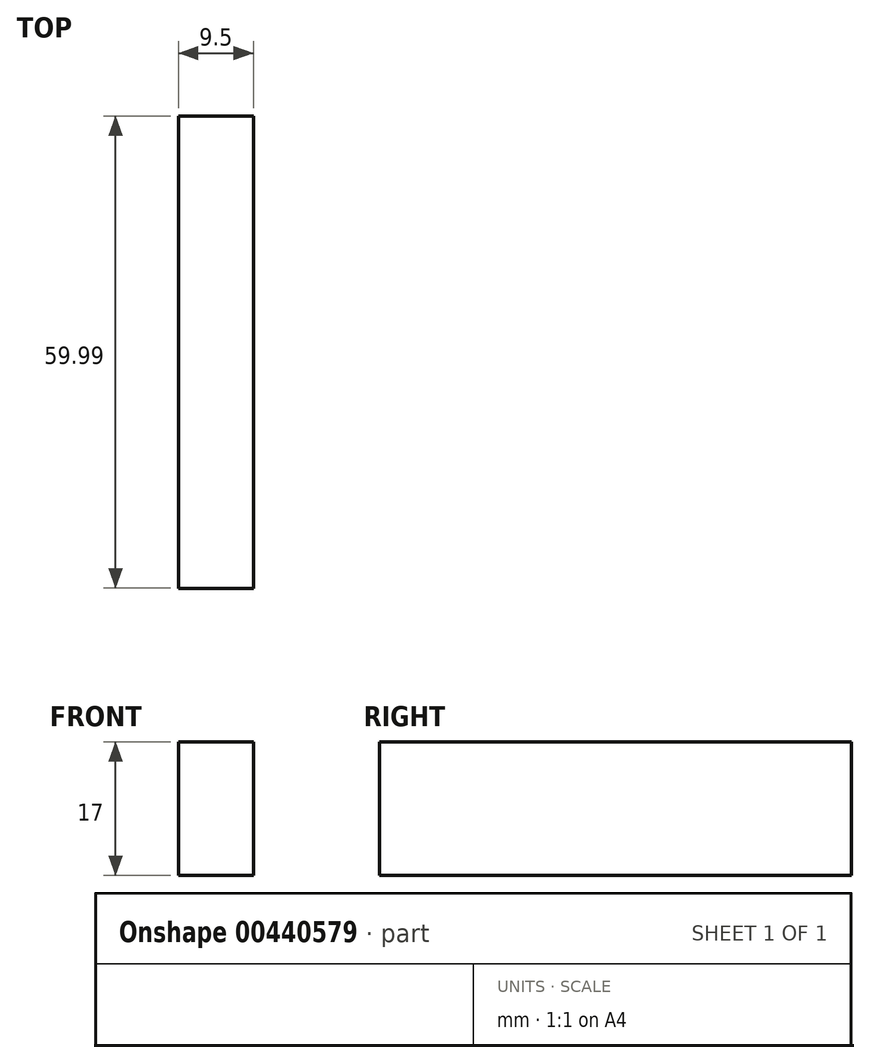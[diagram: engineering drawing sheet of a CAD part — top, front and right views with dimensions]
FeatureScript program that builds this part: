
annotation { "Feature Type Name" : "Feature", "Feature Type Description" : "" }
export const myFeature = defineFeature(function(context is Context, id is Id, definition is map)
    precondition{}
    {
        {
            var Q0;
            Q0=qCreatedBy(makeId("Top.planeOp"),FACE);
            var sketch = newSketch(context, id + "F0", { "sketchPlane" : qUnion([Q0])});
            skArc(sketch, "E0", {"start": v(-453.02, 960.92) * mm, "mid": v(90.35, 1058.5) * mm, "end": v(609.32, 870.25) * mm});
            skLineSegment(sketch, "E1", {"start": v(-465.89, 988.2) * mm, "end": v(-453.02, 960.92) * mm});
            skLineSegment(sketch, "E2", {"start": v(609.32, 870.25) * mm, "end": v(626.62, 894.95) * mm});
            skPoint(sketch, "E3.orphan", {"position": v(-465.89, 988.2) * mm});
            skArc(sketch, "E4", {"start": v(-465.89, 988.2) * mm, "mid": v(92.91, 1088.56) * mm, "end": v(626.62, 894.95) * mm});
            skSolve(sketch);
        }
        {
            var Q0;
            Q0=qCreatedBy(makeId("Top.planeOp"),FACE);
            var sketch = newSketch(context, id + "F1", { "sketchPlane" : qUnion([Q0])});
            skLineSegment(sketch, "E5.bottom", {"start": v(953.2, 454.88) * mm, "end": v(962.7, 454.88) * mm});
            skLineSegment(sketch, "E5.top", {"start": v(953.2, 394.89) * mm, "end": v(962.7, 394.89) * mm});
            skLineSegment(sketch, "E5.left", {"start": v(953.2, 454.88) * mm, "end": v(953.2, 394.89) * mm});
            skLineSegment(sketch, "E5.right", {"start": v(962.7, 454.88) * mm, "end": v(962.7, 394.89) * mm});
            skSolve(sketch);
        }
        {
            var Q0;
            Q0 = qSketchRegion(id + "F1", true);
            extrude(context, id + "F2", {"entities" : qUnion([Q0]), "depth" : 17 * mm});
        }
    });
